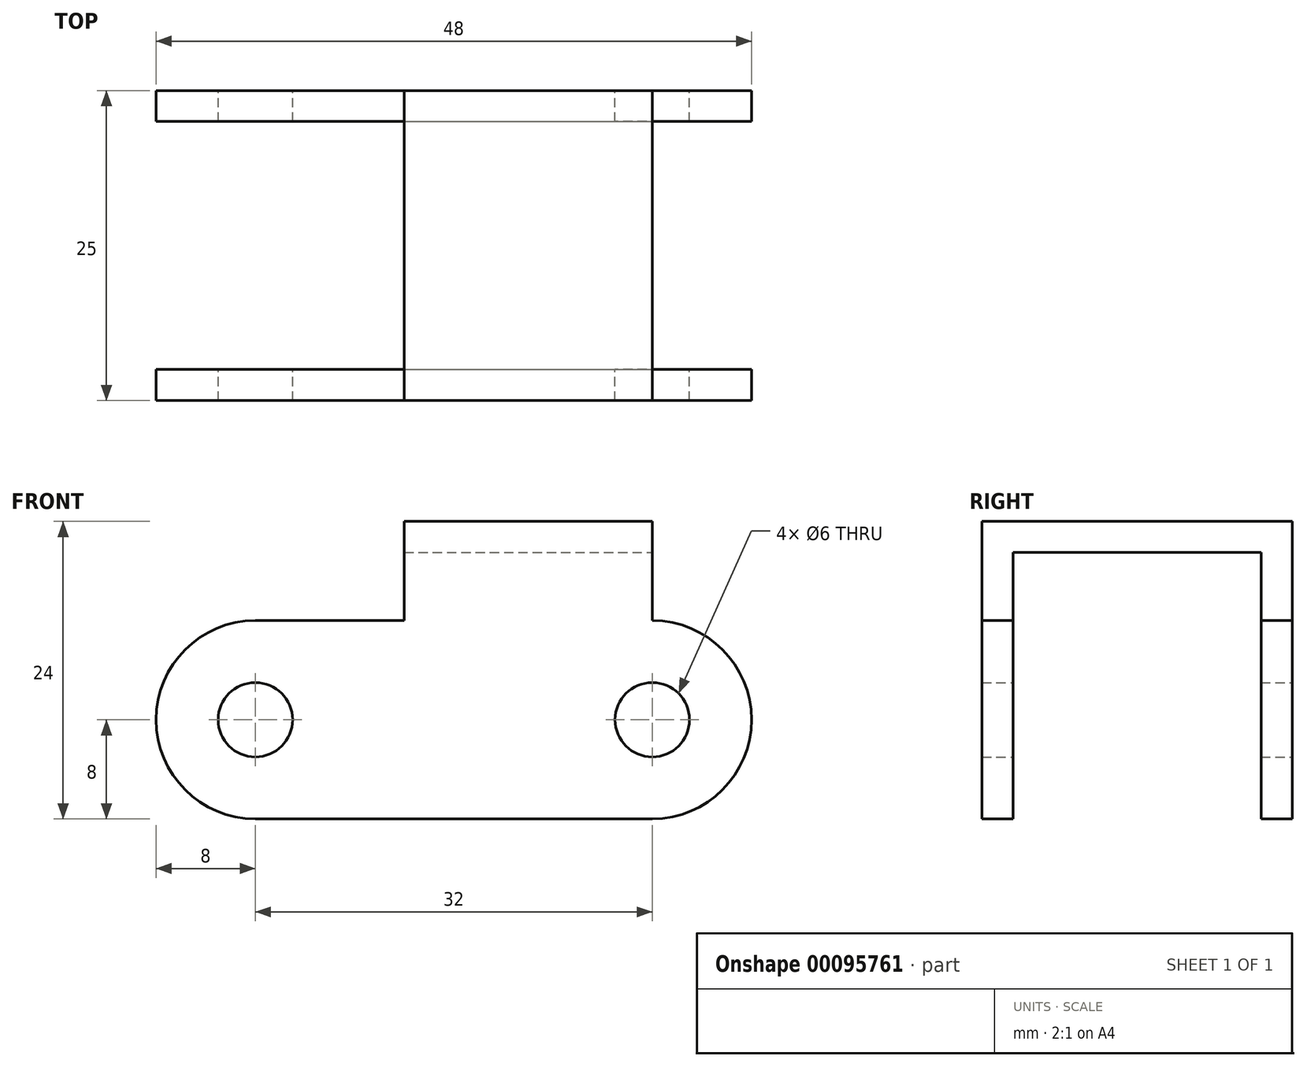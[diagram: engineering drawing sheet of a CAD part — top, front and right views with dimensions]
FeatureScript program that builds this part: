
annotation { "Feature Type Name" : "Feature", "Feature Type Description" : "" }
export const myFeature = defineFeature(function(context is Context, id is Id, definition is map)
    precondition{}
    {
        {
            var Q0;
            Q0=qCreatedBy(makeId("Front.planeOp"),FACE);
            var sketch = newSketch(context, id + "F0", { "sketchPlane" : qUnion([Q0])});
            skLineSegment(sketch, "E0", {"start": v(-20, 16) * mm, "end": v(0, 16) * mm});
            skLineSegment(sketch, "E1", {"start": v(0, 8) * mm, "end": v(0, 16) * mm});
            skLineSegment(sketch, "E2", {"start": v(-20, 16) * mm, "end": v(-20, 8) * mm});
            skLineSegment(sketch, "E3", {"start": v(-20, 8) * mm, "end": v(-32, 8) * mm});
            skArc(sketch, "E4", {"start": v(0, -8) * mm, "mid": v(8, 0) * mm, "end": v(0, 8) * mm});
            skArc(sketch, "E5", {"start": v(-32, 8) * mm, "mid": v(-40, 0) * mm, "end": v(-32, -8) * mm});
            skLineSegment(sketch, "E6", {"start": v(-32, -8) * mm, "end": v(0, -8) * mm});
            skCircle(sketch, "E7", {"center": v(-32, 0) * mm, "radius": 3 * mm});
            skCircle(sketch, "E8", {"center": v(0, 0) * mm, "radius": 3 * mm});
            skSolve(sketch);
        }
        {
            var Q0;
            Q0=makeQuery(id+"F0.imprint","IMPRINT",FACE,{"disambiguationData":[TD([[makeQuery(id+"F0.imprint","IMPRINT",EDGE,{"derivedFrom":sQuery(id+"F0.wireOp",EDGE,"E0")}),-1.0]])]});
            extrude(context, id + "F1", {"entities" : qUnion([Q0]), "depth" : 25 * mm});
        }
        {
            var Q0;
            Q0=makeQuery(id+"F1.opExtrude","SWEPT_FACE",FACE,{"disambiguationData":[OSD([sQuery(id+"F0.wireOp",EDGE,"E7")])]});
            var Q1;
            Q1=makeQuery(id+"F1.opExtrude","SWEPT_FACE",FACE,{"disambiguationData":[OSD([sQuery(id+"F0.wireOp",EDGE,"E8")])]});
            var Q2;
            Q2=makeQuery(id+"F1.opExtrude","SWEPT_FACE",FACE,{"disambiguationData":[OSD([sQuery(id+"F0.wireOp",EDGE,"E6")])]});
            var Q3;
            Q3=makeQuery(id+"F1.opExtrude","SWEPT_FACE",FACE,{"disambiguationData":[OSD([sQuery(id+"F0.wireOp",EDGE,"E5")])]});
            var Q4;
            Q4=makeQuery(id+"F1.opExtrude","SWEPT_FACE",FACE,{"disambiguationData":[OSD([sQuery(id+"F0.wireOp",EDGE,"E4")])]});
            var Q5;
            Q5=makeQuery(id+"F1.opExtrude","SWEPT_FACE",FACE,{"disambiguationData":[OSD([sQuery(id+"F0.wireOp",EDGE,"E3")])]});
            var Q6;
            Q6=makeQuery(id+"F1.opExtrude","SWEPT_FACE",FACE,{"disambiguationData":[OSD([sQuery(id+"F0.wireOp",EDGE,"E1")])]});
            var Q7;
            Q7=makeQuery(id+"F1.opExtrude","SWEPT_FACE",FACE,{"disambiguationData":[OSD([sQuery(id+"F0.wireOp",EDGE,"E2")])]});
            shell(context, id + "F2", {"entities" : qUnion([Q0, Q1, Q2, Q3, Q4, Q5, Q6, Q7]), "thickness" : 2.5 * mm});
        }
    });
